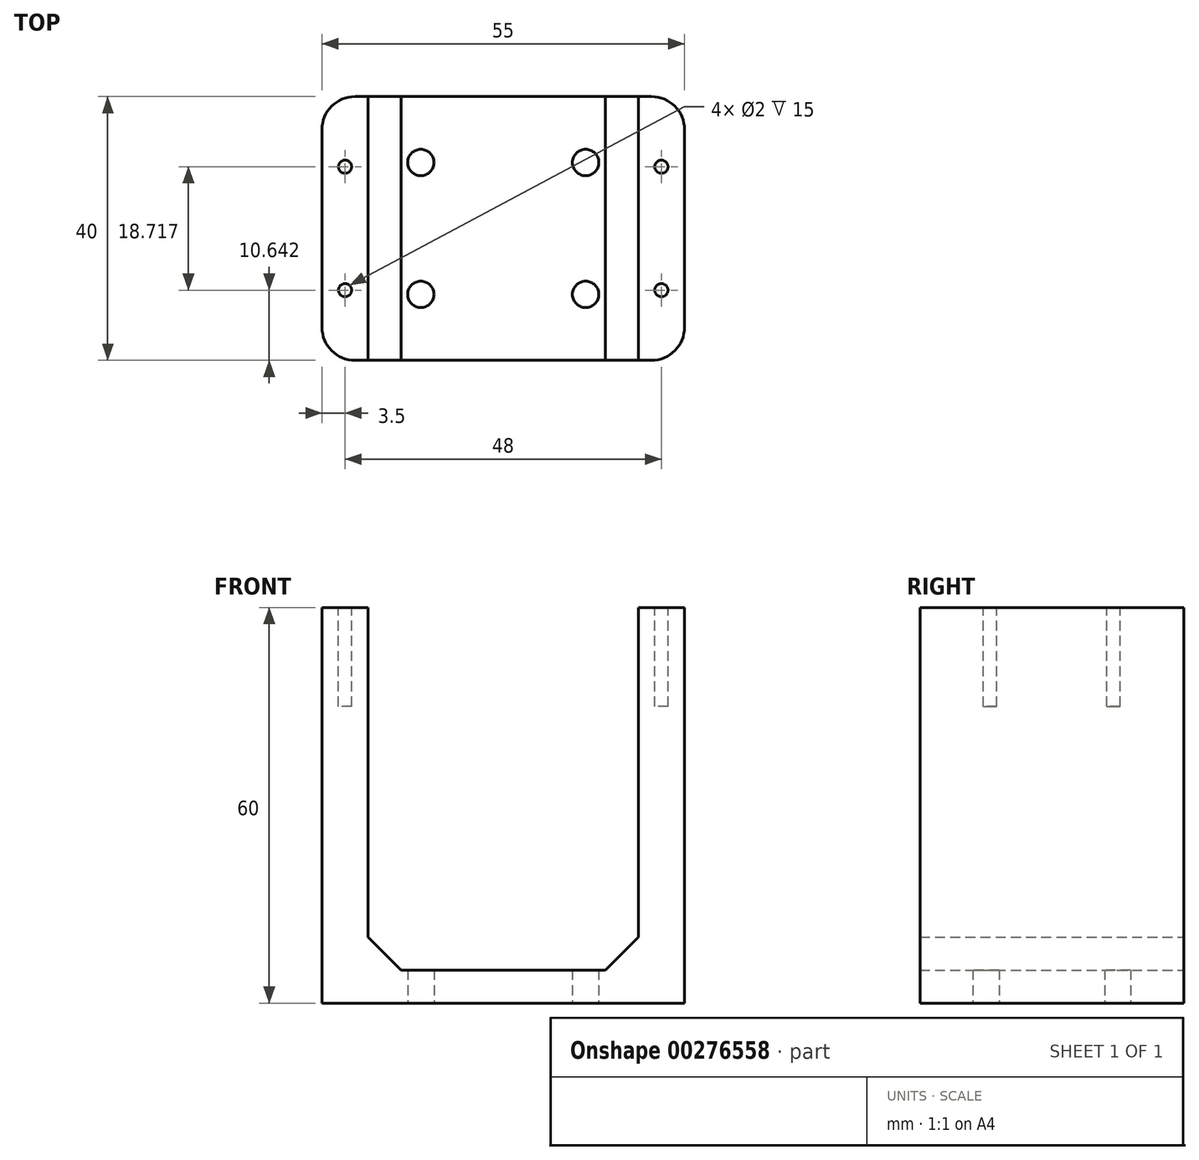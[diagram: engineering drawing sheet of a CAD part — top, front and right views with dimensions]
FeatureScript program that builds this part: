
annotation { "Feature Type Name" : "Feature", "Feature Type Description" : "" }
export const myFeature = defineFeature(function(context is Context, id is Id, definition is map)
    precondition{}
    {
        {
            var Q0;
            Q0=qCreatedBy(makeId("Top.planeOp"),FACE);
            var sketch = newSketch(context, id + "F0", { "sketchPlane" : qUnion([Q0])});
            skLineSegment(sketch, "E0.bottom", {"start": v(27.5, -20) * mm, "end": v(-27.5, -20) * mm});
            skLineSegment(sketch, "E0.top", {"start": v(27.5, 20) * mm, "end": v(-27.5, 20) * mm});
            skLineSegment(sketch, "E0.left", {"start": v(27.5, -20) * mm, "end": v(27.5, 20) * mm});
            skLineSegment(sketch, "E0.right", {"start": v(-27.5, -20) * mm, "end": v(-27.5, 20) * mm});
            skPoint(sketch, "E0.middle", {"position": v(0, 0) * mm});
            skCircle(sketch, "E1", {"center": v(-12.5, 10) * mm, "radius": 2 * mm});
            skCircle(sketch, "E2", {"center": v(12.5, 10) * mm, "radius": 2 * mm});
            skCircle(sketch, "E3", {"center": v(-12.5, -10) * mm, "radius": 2 * mm});
            skCircle(sketch, "E4", {"center": v(12.5, -10) * mm, "radius": 2 * mm});
            skSolve(sketch);
        }
        {
            var Q0;
            Q0 = qSketchRegion(id + "F0", true);
            extrude(context, id + "F1", {"entities" : qUnion([Q0]), "depth" : 5 * mm, "offsetDistance" : 25 * mm});
        }
        {
            var Q0;
            Q0=makeQuery(id+"F1.opExtrude","CAP_FACE",FACE,{"disambiguationData":[OSD([sQuery(id+"F0.wireOp",EDGE,"E0.bottom"),sQuery(id+"F0.wireOp",EDGE,"E0.top"),sQuery(id+"F0.wireOp",EDGE,"E0.left"),sQuery(id+"F0.wireOp",EDGE,"E0.right")])],"isStart":false});
            var sketch = newSketch(context, id + "F2", { "sketchPlane" : qUnion([Q0])});
            skLineSegment(sketch, "E5.bottom", {"start": v(-27.5, 20) * mm, "end": v(-20.5, 20) * mm});
            skLineSegment(sketch, "E5.top", {"start": v(-27.5, -20) * mm, "end": v(-20.5, -20) * mm});
            skLineSegment(sketch, "E5.left", {"start": v(-27.5, 20) * mm, "end": v(-27.5, -20) * mm});
            skLineSegment(sketch, "E5.right", {"start": v(-20.5, 20) * mm, "end": v(-20.5, -20) * mm});
            skLineSegment(sketch, "E6.bottom", {"start": v(27.5, 20) * mm, "end": v(20.5, 20) * mm});
            skLineSegment(sketch, "E6.top", {"start": v(27.5, -20) * mm, "end": v(20.5, -20) * mm});
            skLineSegment(sketch, "E6.left", {"start": v(27.5, 20) * mm, "end": v(27.5, -20) * mm});
            skLineSegment(sketch, "E6.right", {"start": v(20.5, 20) * mm, "end": v(20.5, -20) * mm});
            skSolve(sketch);
        }
        {
            var Q0;
            Q0 = qSketchRegion(id + "F2", true);
            extrude(context, id + "F3", {"entities" : qUnion([Q0]), "operationType" : NewBodyOperationType.ADD, "depth" : 55 * mm, "offsetDistance" : 25 * mm});
        }
        {
            var Q0;
            Q0=makeQuery(id+"F3.opExtrude","CAP_FACE",FACE,{"disambiguationData":[OSD([sQuery(id+"F2.wireOp",EDGE,"E5.bottom"),sQuery(id+"F2.wireOp",EDGE,"E5.top"),sQuery(id+"F2.wireOp",EDGE,"E5.left"),sQuery(id+"F2.wireOp",EDGE,"E5.right")])],"isStart":false});
            var sketch = newSketch(context, id + "F4", { "sketchPlane" : qUnion([Q0])});
            skCircle(sketch, "E7", {"center": v(-24, 9.36) * mm, "radius": 1 * mm});
            skPoint(sketch, "E7.centerSnap0", {"position": v(-24, 20) * mm});
            skCircle(sketch, "E8.MirrorC", {"center": v(24, 9.36) * mm, "radius": 1 * mm});
            skCircle(sketch, "E9.MirrorC", {"center": v(24, -9.36) * mm, "radius": 1 * mm});
            skCircle(sketch, "E10.MirrorC", {"center": v(-24, -9.36) * mm, "radius": 1 * mm});
            skSolve(sketch);
        }
        {
            var Q0;
            Q0 = qSketchRegion(id + "F4", true);
            extrude(context, id + "F5", {"entities" : qUnion([Q0]), "operationType" : NewBodyOperationType.REMOVE, "oppositeDirection" : true, "depth" : 15 * mm, "offsetDistance" : 25 * mm});
        }
        {
            var Q0;
            Q0=makeQuery(id+"F3.boolean.opBoolean","MERGE",EDGE,{"derivedFrom":[makeQuery(id+"F1.opExtrude","SWEPT_EDGE",EDGE,{"disambiguationData":[OSD([sQuery(id+"F0.wireOp",EDGE,"E0.top"),sQuery(id+"F0.wireOp",EDGE,"E0.right")])]}),makeQuery(id+"F3.opExtrude","SWEPT_EDGE",EDGE,{"disambiguationData":[OSD([sQuery(id+"F2.wireOp",EDGE,"E5.bottom"),sQuery(id+"F2.wireOp",EDGE,"E5.left")])]})]});
            var Q1;
            Q1=makeQuery(id+"F3.boolean.opBoolean","MERGE",EDGE,{"derivedFrom":[makeQuery(id+"F1.opExtrude","SWEPT_EDGE",EDGE,{"disambiguationData":[OSD([sQuery(id+"F0.wireOp",EDGE,"E0.bottom"),sQuery(id+"F0.wireOp",EDGE,"E0.right")])]}),makeQuery(id+"F3.opExtrude","SWEPT_EDGE",EDGE,{"disambiguationData":[OSD([sQuery(id+"F2.wireOp",EDGE,"E5.top"),sQuery(id+"F2.wireOp",EDGE,"E5.left")])]})]});
            var Q2;
            Q2=makeQuery(id+"F3.boolean.opBoolean","MERGE",EDGE,{"derivedFrom":[makeQuery(id+"F1.opExtrude","SWEPT_EDGE",EDGE,{"disambiguationData":[OSD([sQuery(id+"F0.wireOp",EDGE,"E0.bottom"),sQuery(id+"F0.wireOp",EDGE,"E0.left")])]}),makeQuery(id+"F3.opExtrude","SWEPT_EDGE",EDGE,{"disambiguationData":[OSD([sQuery(id+"F2.wireOp",EDGE,"E6.top"),sQuery(id+"F2.wireOp",EDGE,"E6.left")])]})]});
            var Q3;
            Q3=makeQuery(id+"F3.boolean.opBoolean","MERGE",EDGE,{"derivedFrom":[makeQuery(id+"F1.opExtrude","SWEPT_EDGE",EDGE,{"disambiguationData":[OSD([sQuery(id+"F0.wireOp",EDGE,"E0.top"),sQuery(id+"F0.wireOp",EDGE,"E0.left")])]}),makeQuery(id+"F3.opExtrude","SWEPT_EDGE",EDGE,{"disambiguationData":[OSD([sQuery(id+"F2.wireOp",EDGE,"E6.bottom"),sQuery(id+"F2.wireOp",EDGE,"E6.left")])]})]});
            fillet(context, id + "F6", {"entities" : qUnion([Q0, Q1, Q2, Q3]), "tangentPropagation" : true, "radius" : 5 * mm, "defaultsChanged" : false, "vertexSettings" : [], "allowEdgeOverflow" : false});
        }
        {
            var Q0;
            Q0=makeQuery(id+"F3.boolean.opBoolean","MERGE",FACE,{"derivedFrom":[makeQuery(id+"F1.opExtrude","SWEPT_FACE",FACE,{"disambiguationData":[OSD([sQuery(id+"F0.wireOp",EDGE,"E0.top")])]}),makeQuery(id+"F3.opExtrude","SWEPT_FACE",FACE,{"disambiguationData":[OSD([sQuery(id+"F2.wireOp",EDGE,"E5.bottom")])]}),makeQuery(id+"F3.opExtrude","SWEPT_FACE",FACE,{"disambiguationData":[OSD([sQuery(id+"F2.wireOp",EDGE,"E6.bottom")])]})]});
            var sketch = newSketch(context, id + "F7", { "sketchPlane" : qUnion([Q0])});
            skLineSegment(sketch, "E11.bottom", {"start": v(-20.5, 5) * mm, "end": v(-15.5, 5) * mm});
            skLineSegment(sketch, "E11.top", {"start": v(-20.5, 10) * mm, "end": v(-15.5, 10) * mm});
            skLineSegment(sketch, "E11.left", {"start": v(-20.5, 5) * mm, "end": v(-20.5, 10) * mm});
            skLineSegment(sketch, "E11.right", {"start": v(-15.5, 5) * mm, "end": v(-15.5, 10) * mm});
            skLineSegment(sketch, "E12.MirrorCS", {"start": v(20.5, 10) * mm, "end": v(15.5, 10) * mm});
            skLineSegment(sketch, "E13.MirrorCS", {"start": v(15.5, 5) * mm, "end": v(15.5, 10) * mm});
            skLineSegment(sketch, "E14.MirrorCS", {"start": v(20.5, 5) * mm, "end": v(15.5, 5) * mm});
            skLineSegment(sketch, "E15.MirrorCS", {"start": v(20.5, 5) * mm, "end": v(20.5, 10) * mm});
            skSolve(sketch);
        }
        {
            var Q0;
            Q0 = qSketchRegion(id + "F7", true);
            extrude(context, id + "F8", {"entities" : qUnion([Q0]), "operationType" : NewBodyOperationType.ADD, "oppositeDirection" : true, "depth" : 40 * mm, "offsetDistance" : 25 * mm});
        }
        {
            var Q0;
            Q0=makeQuery(id+"F8.opExtrude","SWEPT_EDGE",EDGE,{"disambiguationData":[OSD([sQuery(id+"F7.wireOp",EDGE,"E11.top"),sQuery(id+"F7.wireOp",EDGE,"E11.right")])]});
            var Q1;
            Q1=makeQuery(id+"F8.opExtrude","SWEPT_EDGE",EDGE,{"disambiguationData":[OSD([sQuery(id+"F7.wireOp",EDGE,"E12.MirrorCS"),sQuery(id+"F7.wireOp",EDGE,"E13.MirrorCS")])]});
            chamfer(context, id + "F9", {"entities" : qUnion([Q0, Q1]), "width" : 5 * mm, "tangentPropagation" : true});
        }
    });
